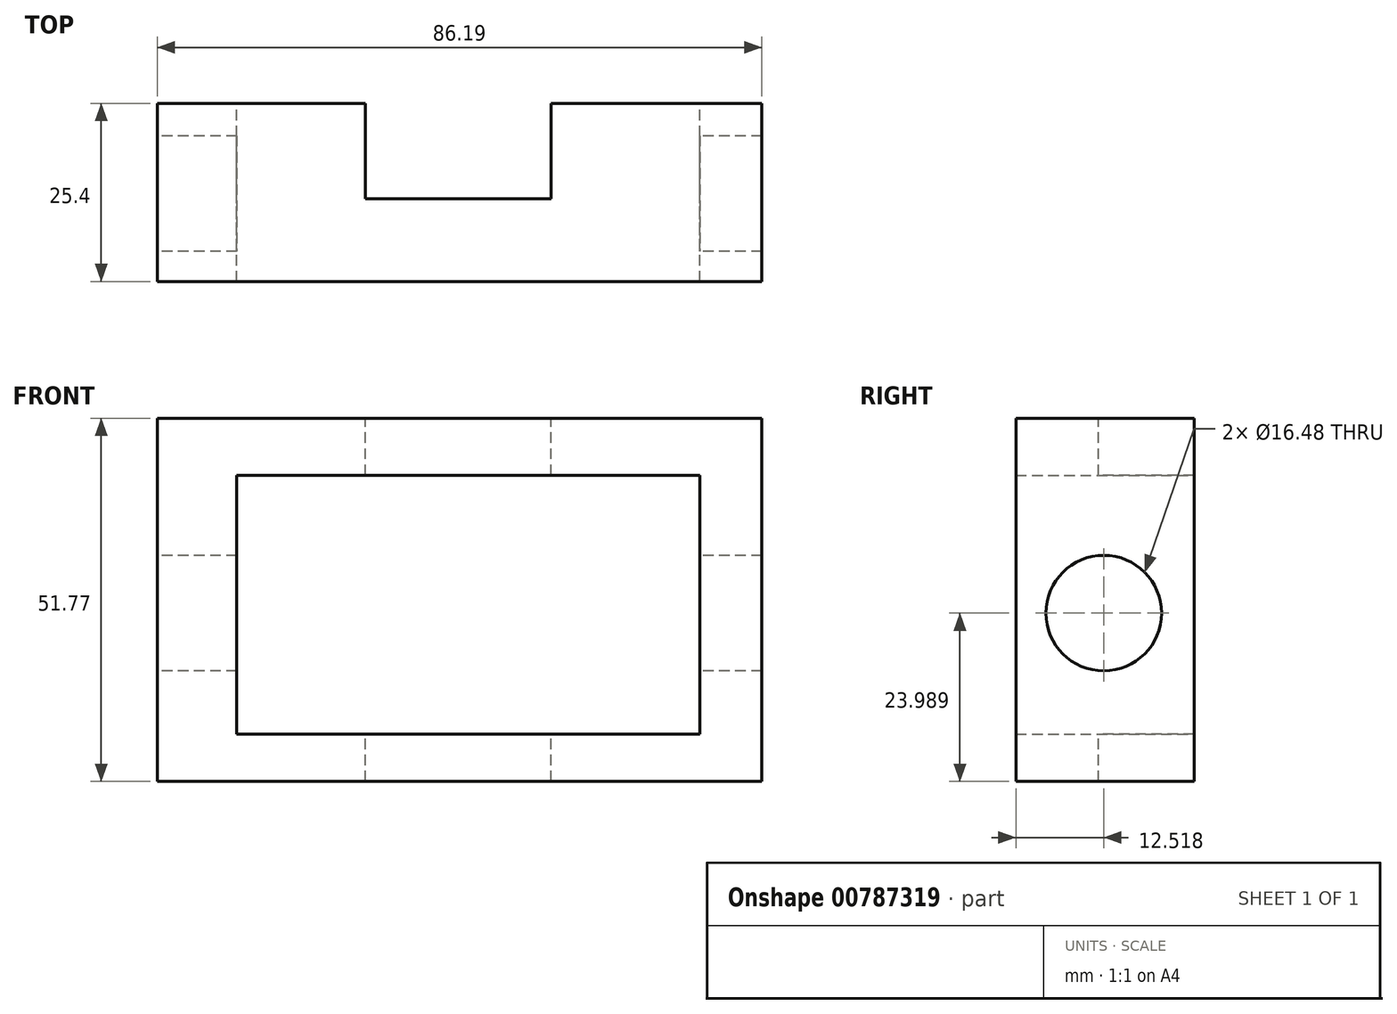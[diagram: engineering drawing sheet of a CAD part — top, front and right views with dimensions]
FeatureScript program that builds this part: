
annotation { "Feature Type Name" : "Feature", "Feature Type Description" : "" }
export const myFeature = defineFeature(function(context is Context, id is Id, definition is map)
    precondition{}
    {
        {
            var Q0;
            Q0=qCreatedBy(makeId("Front.planeOp"),FACE);
            var sketch = newSketch(context, id + "F0", { "sketchPlane" : qUnion([Q0])});
            skLineSegment(sketch, "E0.bottom", {"start": v(-28.8, -16.5) * mm, "end": v(37.23, -16.5) * mm});
            skLineSegment(sketch, "E0.top", {"start": v(-28.8, -9.76) * mm, "end": v(37.23, -9.76) * mm});
            skLineSegment(sketch, "E0.left", {"start": v(-28.8, -16.5) * mm, "end": v(-28.8, -9.76) * mm});
            skLineSegment(sketch, "E0.right", {"start": v(37.23, -16.5) * mm, "end": v(37.23, -9.76) * mm});
            skLineSegment(sketch, "E1.bottom", {"start": v(-28.8, -16.5) * mm, "end": v(-40.14, -16.5) * mm});
            skLineSegment(sketch, "E1.top", {"start": v(-28.8, 27.15) * mm, "end": v(-40.14, 27.15) * mm});
            skLineSegment(sketch, "E1.left", {"start": v(-28.8, -16.5) * mm, "end": v(-28.8, 27.15) * mm});
            skLineSegment(sketch, "E1.right", {"start": v(-40.14, -16.5) * mm, "end": v(-40.14, 27.15) * mm});
            skLineSegment(sketch, "E2.bottom", {"start": v(-40.14, 27.15) * mm, "end": v(37.23, 27.15) * mm});
            skLineSegment(sketch, "E2.top", {"start": v(-40.14, 35.26) * mm, "end": v(37.23, 35.26) * mm});
            skLineSegment(sketch, "E2.left", {"start": v(-40.14, 27.15) * mm, "end": v(-40.14, 35.26) * mm});
            skLineSegment(sketch, "E2.right", {"start": v(37.23, 27.15) * mm, "end": v(37.23, 35.26) * mm});
            skLineSegment(sketch, "E3.bottom", {"start": v(37.23, 35.26) * mm, "end": v(46.05, 35.26) * mm});
            skLineSegment(sketch, "E3.top", {"start": v(37.23, -16.5) * mm, "end": v(46.05, -16.5) * mm});
            skLineSegment(sketch, "E3.left", {"start": v(37.23, 35.26) * mm, "end": v(37.23, -16.5) * mm});
            skLineSegment(sketch, "E3.right", {"start": v(46.05, 35.26) * mm, "end": v(46.05, -16.5) * mm});
            skSolve(sketch);
        }
        {
            var Q0;
            {var subQ1=makeQuery(id+"F0.imprint","IMPRINT",EDGE,{"derivedFrom":sQuery(id+"F0.wireOp",EDGE,"E0.right")});var subQ2=makeQuery(id+"F0.imprint","IMPRINT",EDGE,{"derivedFrom":sQuery(id+"F0.wireOp",EDGE,"E1.top")});var subQ3=makeQuery(id+"F0.imprint","IMPRINT",EDGE,{"derivedFrom":sQuery(id+"F0.wireOp",EDGE,"E0.left")});Q0=qUnion([makeQuery(id+"F0.imprint","IMPRINT",FACE,{"disambiguationData":[TD([[subQ2,-1.0]])]}),makeQuery(id+"F0.imprint","IMPRINT",FACE,{"disambiguationData":[TD([[makeQuery(id+"F0.imprint","IMPRINT",EDGE,{"derivedFrom":sQuery(id+"F0.wireOp",EDGE,"E0.bottom")}),1.0]])]}),makeQuery(id+"F0.imprint","IMPRINT",FACE,{"disambiguationData":[TD([[subQ3,1.0]])]}),makeQuery(id+"F0.imprint","IMPRINT",FACE,{"disambiguationData":[TD([[subQ1,-1.0]])]})]);}
            extrude(context, id + "F1", {"entities" : qUnion([Q0]), "depth" : 25.4 * mm, "offsetDistance" : 25.4 * mm});
        }
        {
            var Q0;
            {var subQ1=makeQuery(id+"F0.imprint","IMPRINT",EDGE,{"derivedFrom":sQuery(id+"F0.wireOp",EDGE,"E0.right")});var subQ2=makeQuery(id+"F0.imprint","IMPRINT",EDGE,{"derivedFrom":sQuery(id+"F0.wireOp",EDGE,"E1.top")});var subQ3=makeQuery(id+"F0.imprint","IMPRINT",EDGE,{"derivedFrom":sQuery(id+"F0.wireOp",EDGE,"E0.left")});Q0=qUnion([makeQuery(id+"F0.imprint","IMPRINT",FACE,{"disambiguationData":[TD([[subQ2,-1.0]])]}),makeQuery(id+"F0.imprint","IMPRINT",FACE,{"disambiguationData":[TD([[makeQuery(id+"F0.imprint","IMPRINT",EDGE,{"derivedFrom":sQuery(id+"F0.wireOp",EDGE,"E0.bottom")}),1.0]])]}),makeQuery(id+"F0.imprint","IMPRINT",FACE,{"disambiguationData":[TD([[subQ3,1.0]])]}),makeQuery(id+"F0.imprint","IMPRINT",FACE,{"disambiguationData":[TD([[subQ1,-1.0]])]})]);}
            extrude(context, id + "F2", {"entities" : qUnion([Q0]), "operationType" : NewBodyOperationType.ADD, "depth" : 25.4 * mm, "offsetDistance" : 25.4 * mm});
        }
        {
            var Q0;
            Q0=makeQuery(id+"F1.opExtrude","SWEPT_FACE",FACE,{"disambiguationData":[OSD([sQuery(id+"F0.wireOp",EDGE,"E2.top"),sQuery(id+"F0.wireOp",EDGE,"E3.bottom")])]});
            var sketch = newSketch(context, id + "F3", { "sketchPlane" : qUnion([Q0])});
            skLineSegment(sketch, "E4.bottom", {"start": v(-10.48, 0) * mm, "end": v(16.03, 0) * mm});
            skLineSegment(sketch, "E4.top", {"start": v(-10.48, -13.62) * mm, "end": v(16.03, -13.62) * mm});
            skLineSegment(sketch, "E4.left", {"start": v(-10.48, 0) * mm, "end": v(-10.48, -13.62) * mm});
            skLineSegment(sketch, "E4.right", {"start": v(16.03, 0) * mm, "end": v(16.03, -13.62) * mm});
            skSolve(sketch);
        }
        {
            var Q0;
            Q0=makeQuery(id+"F3.imprint","IMPRINT",FACE,{"disambiguationData":[TD([[makeQuery(id+"F3.imprint","IMPRINT",EDGE,{"derivedFrom":sQuery(id+"F3.wireOp",EDGE,"E4.bottom")}),-1.0]])]});
            extrude(context, id + "F4", {"entities" : qUnion([Q0]), "operationType" : NewBodyOperationType.REMOVE, "oppositeDirection" : true, "depth" : 76.45 * mm, "offsetDistance" : 25.4 * mm});
        }
        {
            var Q0;
            Q0=makeQuery(id+"F1.opExtrude","SWEPT_FACE",FACE,{"disambiguationData":[OSD([sQuery(id+"F0.wireOp",EDGE,"E1.right"),sQuery(id+"F0.wireOp",EDGE,"E2.left")])]});
            var sketch = newSketch(context, id + "F5", { "sketchPlane" : qUnion([Q0])});
            skCircle(sketch, "E5", {"center": v(12.88, 7.48) * mm, "radius": 8.24 * mm});
            skSolve(sketch);
        }
        {
            var Q0;
            Q0=makeQuery(id+"F5.imprint","IMPRINT",FACE,{"disambiguationData":[TD([[makeQuery(id+"F5.imprint","IMPRINT",EDGE,{"derivedFrom":sQuery(id+"F5.wireOp",EDGE,"E5")}),1.0]])]});
            extrude(context, id + "F6", {"entities" : qUnion([Q0]), "operationType" : NewBodyOperationType.REMOVE, "oppositeDirection" : true, "depth" : 155.2 * mm, "offsetDistance" : 25.4 * mm});
        }
    });
